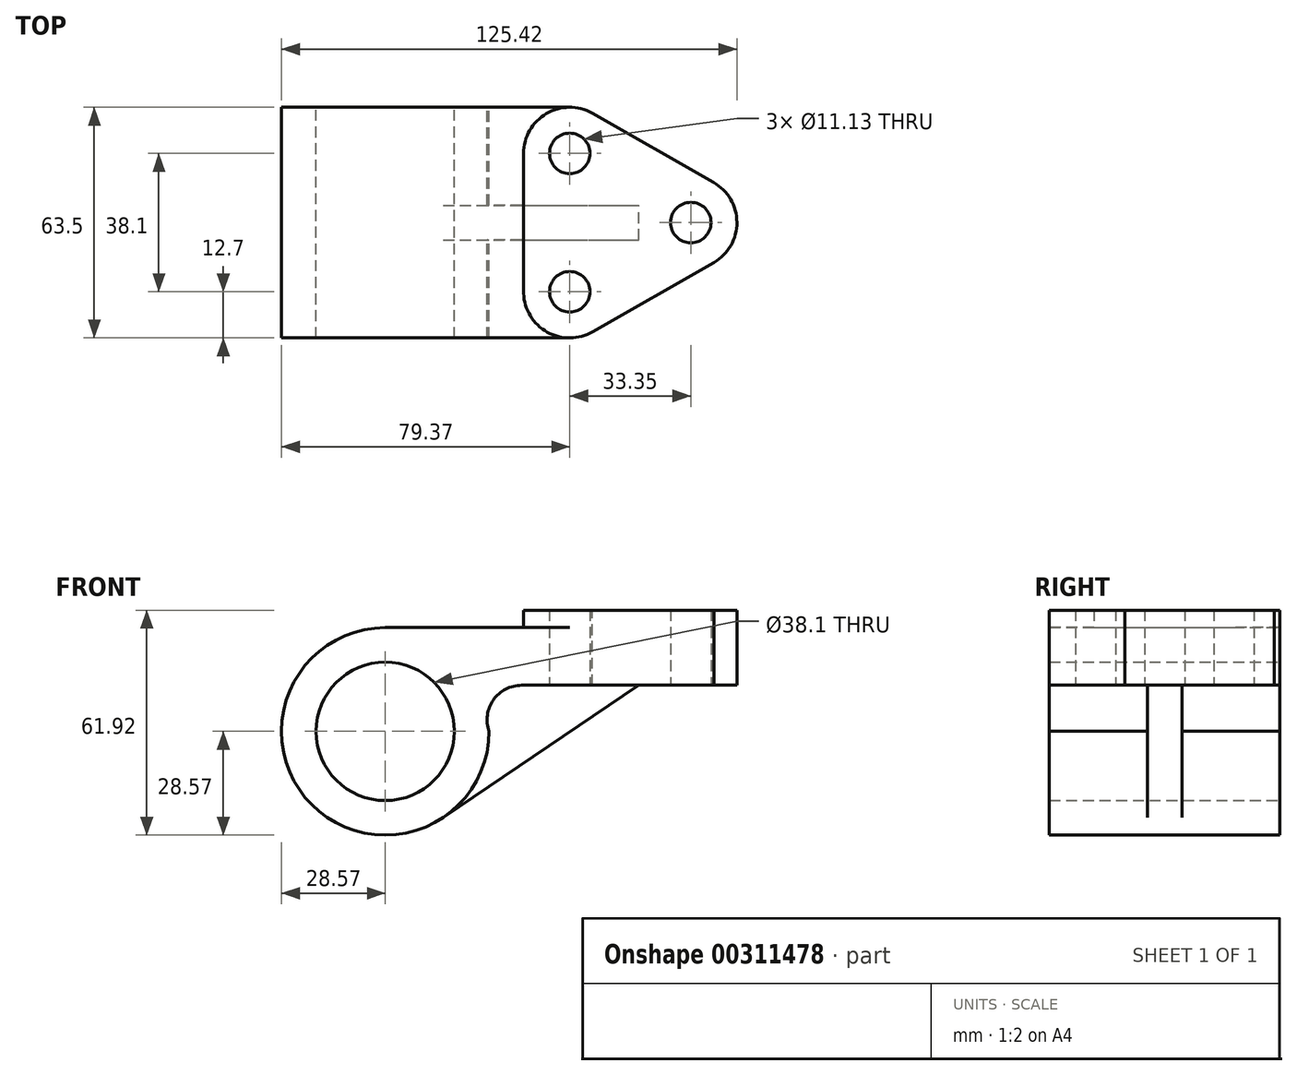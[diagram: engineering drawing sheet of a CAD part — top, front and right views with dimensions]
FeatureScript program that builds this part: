
annotation { "Feature Type Name" : "Feature", "Feature Type Description" : "" }
export const myFeature = defineFeature(function(context is Context, id is Id, definition is map)
    precondition{}
    {
        {
            var Q0;
            Q0=qCreatedBy(makeId("Front.planeOp"),FACE);
            var sketch = newSketch(context, id + "F0", { "sketchPlane" : qUnion([Q0])});
            skCircle(sketch, "E0", {"center": v(0, 0) * mm, "radius": 19.05 * mm});
            skArc(sketch, "E1", {"start": v(0, 28.58) * mm, "mid": v(-20.2, -20.2) * mm, "end": v(28.58, 0) * mm});
            skLineSegment(sketch, "E2", {"start": v(0, 28.58) * mm, "end": v(102.14, 28.58) * mm});
            skLineSegment(sketch, "E3", {"start": v(37.56, 12.7) * mm, "end": v(102.14, 12.7) * mm});
            skLineSegment(sketch, "E4", {"start": v(102.14, 28.58) * mm, "end": v(102.14, 12.7) * mm});
            skLineSegment(sketch, "E5", {"start": v(16, -23.68) * mm, "end": v(69.85, 12.7) * mm});
            skArc(sketch, "E6", {"start": v(37.56, 12.7) * mm, "mid": v(29.78, 8.67) * mm, "end": v(28.58, 0) * mm});
            skSolve(sketch);
        }
        {
            var Q0;
            Q0=makeQuery(id+"F0.imprint","IMPRINT",FACE,{"disambiguationData":[TD([[makeQuery(id+"F0.imprint","IMPRINT",EDGE,{"derivedFrom":sQuery(id+"F0.wireOp",EDGE,"E0")}),-1.0]])]});
            extrude(context, id + "F1", {"entities" : qUnion([Q0]), "endBound" : BoundingType.SYMMETRIC, "depth" : 63.5 * mm});
        }
        {
            var Q0;
            {var subQ2=sQuery(id+"F0.wireOp",EDGE,"E5");Q0=makeQuery(id+"F0.imprint","IMPRINT",FACE,{"disambiguationData":[TD([[makeQuery(id+"F0.imprint","IMPRINT",EDGE,{"derivedFrom":subQ2}),1.0]])]});}
            extrude(context, id + "F2", {"entities" : qUnion([Q0]), "operationType" : NewBodyOperationType.ADD, "endBound" : BoundingType.SYMMETRIC, "depth" : 9.52 * mm});
        }
        {
            var Q0;
            Q0=makeQuery(id+"F1.opExtrude","SWEPT_FACE",FACE,{"disambiguationData":[OSD([sQuery(id+"F0.wireOp",EDGE,"E2")])]});
            var sketch = newSketch(context, id + "F3", { "sketchPlane" : qUnion([Q0])});
            skCircle(sketch, "E7", {"center": v(84.15, 0) * mm, "radius": 5.56 * mm});
            skCircle(sketch, "E8", {"center": v(50.8, 19.05) * mm, "radius": 5.56 * mm});
            skCircle(sketch, "E9", {"center": v(50.8, -19.05) * mm, "radius": 5.56 * mm});
            skLineSegment(sketch, "E10", {"start": v(0, 0) * mm, "end": v(164.2, 0) * mm, "construction": true});
            skArc(sketch, "E11.filletArc", {"start": v(56.98, 30.14) * mm, "mid": v(44.37, 30) * mm, "end": v(38.1, 19.05) * mm});
            skArc(sketch, "E12.filletArc", {"start": v(38.1, -19.5) * mm, "mid": v(44.62, -30.14) * mm, "end": v(57.1, -30.08) * mm});
            skArc(sketch, "E13.filletArc", {"start": v(90.57, -10.96) * mm, "mid": v(96.85, 0.07) * mm, "end": v(90.45, 11.03) * mm});
            skLineSegment(sketch, "E14", {"start": v(56.98, 30.14) * mm, "end": v(90.45, 11.03) * mm});
            skLineSegment(sketch, "E15", {"start": v(90.57, -10.96) * mm, "end": v(57.1, -30.08) * mm});
            skLineSegment(sketch, "E16", {"start": v(38.1, -19.5) * mm, "end": v(38.1, 19.05) * mm});
            skSolve(sketch);
        }
        {
            var Q0;
            Q0=makeQuery(id+"F3.imprint","IMPRINT",FACE,{"disambiguationData":[TD([[makeQuery(id+"F3.imprint","IMPRINT",EDGE,{"derivedFrom":sQuery(id+"F3.wireOp",EDGE,"E13.filletArc")}),-1.0]])]});
            extrude(context, id + "F4", {"entities" : qUnion([Q0]), "operationType" : NewBodyOperationType.REMOVE, "oppositeDirection" : true, "depth" : 25.4 * mm});
        }
        {
            var Q0;
            Q0 = qSketchRegion(id + "F3", true);
            extrude(context, id + "F5", {"entities" : qUnion([Q0]), "operationType" : NewBodyOperationType.ADD, "depth" : 4.78 * mm});
        }
        {
            var Q0;
            Q0=makeQuery(id+"F3.imprint","IMPRINT",FACE,{"disambiguationData":[TD([[makeQuery(id+"F3.imprint","IMPRINT",EDGE,{"derivedFrom":sQuery(id+"F3.wireOp",EDGE,"E8")}),1.0]])]});
            var Q1;
            Q1=makeQuery(id+"F3.imprint","IMPRINT",FACE,{"disambiguationData":[TD([[makeQuery(id+"F3.imprint","IMPRINT",EDGE,{"derivedFrom":sQuery(id+"F3.wireOp",EDGE,"E7")}),1.0]])]});
            var Q2;
            Q2=makeQuery(id+"F3.imprint","IMPRINT",FACE,{"disambiguationData":[TD([[makeQuery(id+"F3.imprint","IMPRINT",EDGE,{"derivedFrom":sQuery(id+"F3.wireOp",EDGE,"E9")}),1.0]])]});
            extrude(context, id + "F6", {"entities" : qUnion([Q0, Q1, Q2]), "operationType" : NewBodyOperationType.REMOVE, "endBound" : BoundingType.THROUGH_ALL, "oppositeDirection" : true, "depth" : 25.4 * mm});
        }
    });
